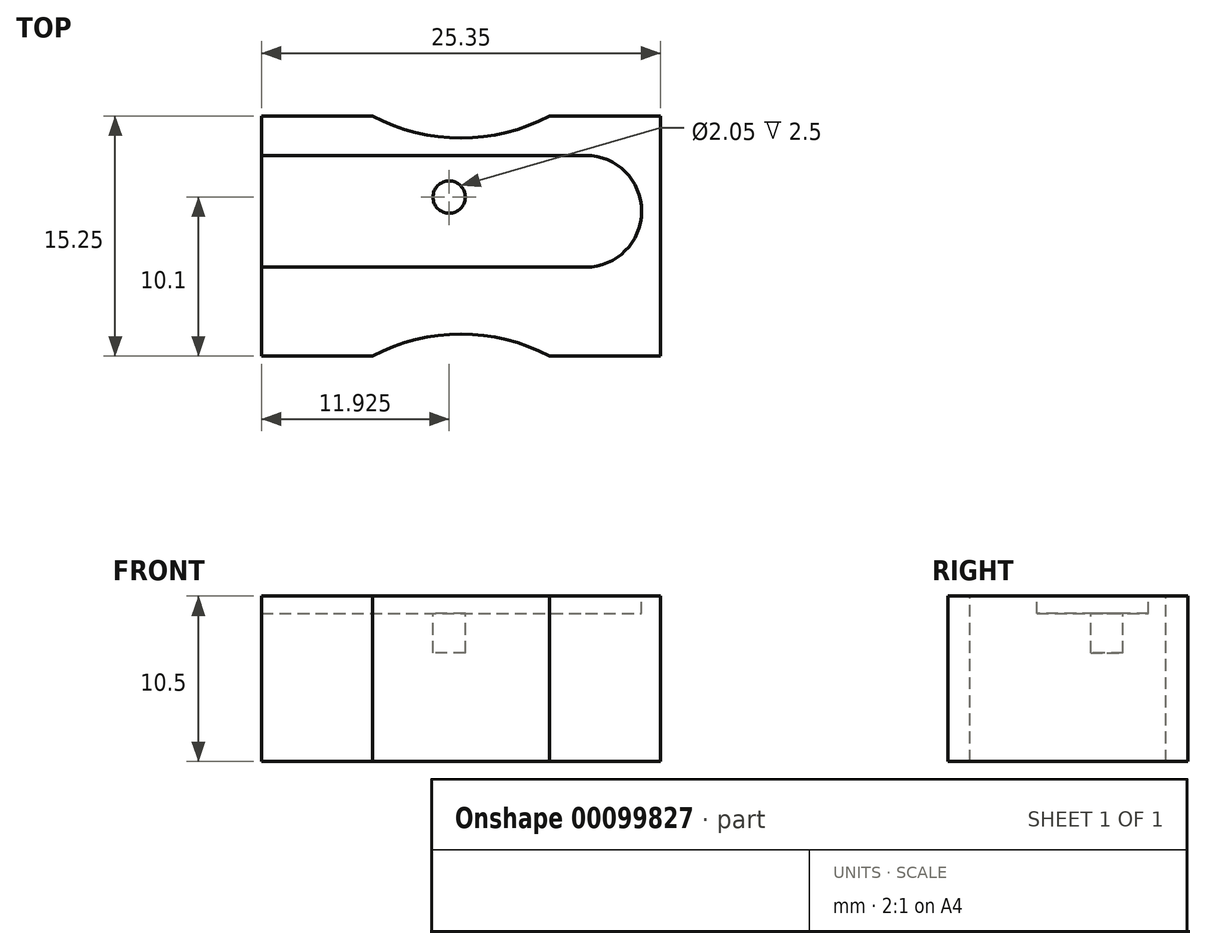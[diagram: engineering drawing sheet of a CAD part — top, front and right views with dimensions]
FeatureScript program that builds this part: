
annotation { "Feature Type Name" : "Feature", "Feature Type Description" : "" }
export const myFeature = defineFeature(function(context is Context, id is Id, definition is map)
    precondition{}
    {
        {
            var Q0;
            Q0=qCreatedBy(makeId("Top.planeOp"),FACE);
            var sketch = newSketch(context, id + "F0", { "sketchPlane" : qUnion([Q0])});
            skLineSegment(sketch, "E0.bottom", {"start": v(0, 0) * mm, "end": v(-7.05, 0) * mm});
            skLineSegment(sketch, "E0.top", {"start": v(0, 15.25) * mm, "end": v(-7.05, 15.25) * mm});
            skArc(sketch, "E1", {"start": v(-7.05, 0) * mm, "mid": v(-12.68, 1.4) * mm, "end": v(-18.3, 0) * mm});
            skLineSegment(sketch, "E2.trimOffspring", {"start": v(-18.3, 15.25) * mm, "end": v(-25.35, 15.25) * mm});
            skLineSegment(sketch, "E3.trimOffspring", {"start": v(-18.3, 0) * mm, "end": v(-25.35, 0) * mm});
            skLineSegment(sketch, "E4", {"start": v(-25.35, 15.25) * mm, "end": v(-25.35, 0) * mm});
            skLineSegment(sketch, "E5", {"start": v(0, 0) * mm, "end": v(0, 15.25) * mm});
            skArc(sketch, "E6", {"start": v(-18.3, 15.25) * mm, "mid": v(-12.68, 13.86) * mm, "end": v(-7.05, 15.25) * mm});
            skLineSegment(sketch, "E7", {"start": v(-25.35, 12.75) * mm, "end": v(-4.75, 12.75) * mm});
            skLineSegment(sketch, "E8", {"start": v(-25.35, 5.65) * mm, "end": v(-4.75, 5.65) * mm});
            skArc(sketch, "E9", {"start": v(-4.75, 5.65) * mm, "mid": v(-1.2, 9.2) * mm, "end": v(-4.75, 12.75) * mm});
            skSolve(sketch);
        }
        {
            var Q0;
            Q0 = qSketchRegion(id + "F0", true);
            extrude(context, id + "F1", {"entities" : qUnion([Q0]), "oppositeDirection" : true, "depth" : 10.5 * mm});
        }
        {
            var Q0;
            {var subQ0=sQuery(id+"F0.wireOp",EDGE,"E7");Q0=makeQuery(id+"F0.imprint","IMPRINT",FACE,{"disambiguationData":[TD([[makeQuery(id+"F0.imprint","IMPRINT",EDGE,{"derivedFrom":subQ0}),-1.0]])]});}
            extrude(context, id + "F2", {"entities" : qUnion([Q0]), "operationType" : NewBodyOperationType.REMOVE, "oppositeDirection" : true, "depth" : 1.1 * mm});
        }
        {
            var Q0;
            Q0=makeQuery(id+"F2.boolean.opBoolean","COPY",FACE,{"derivedFrom":makeQuery(id+"F2.opExtrude","CAP_FACE",FACE,{"disambiguationData":[OSD([sQuery(id+"F0.wireOp",EDGE,"E4"),sQuery(id+"F0.wireOp",EDGE,"E7"),sQuery(id+"F0.wireOp",EDGE,"E8"),sQuery(id+"F0.wireOp",EDGE,"E9")])],"isStart":false})});
            var sketch = newSketch(context, id + "F3", { "sketchPlane" : qUnion([Q0])});
            skCircle(sketch, "E10", {"center": v(-13.42, 10.1) * mm, "radius": 1.02 * mm});
            skSolve(sketch);
        }
        {
            var Q0;
            Q0=makeQuery(id+"F3.imprint","IMPRINT",FACE,{"disambiguationData":[TD([[makeQuery(id+"F3.imprint","IMPRINT",EDGE,{"derivedFrom":sQuery(id+"F3.wireOp",EDGE,"E10")}),1.0]])]});
            extrude(context, id + "F4", {"entities" : qUnion([Q0]), "operationType" : NewBodyOperationType.REMOVE, "oppositeDirection" : true, "depth" : 2.5 * mm});
        }
    });
